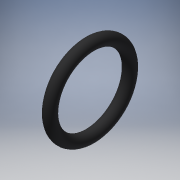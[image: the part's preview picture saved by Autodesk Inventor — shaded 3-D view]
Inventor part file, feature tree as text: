
AUTODESK INVENTOR PART (.ipt)
format: ipt  version: 2019.4 (Build 234330000, 330)  size: 146,432 bytes
history: native  units: in
note: dims shown in document units (in); Inventor stores cm internally (conversion verified against a paired STEP export)
features: sketch x2, sweep x1
ambient origin geometry x8: Origin, YZ Plane, XZ Plane, XY Plane, X Axis, Y Axis, Z Axis, Center Point
bodies: Solid1 (feature_tree)
feature tree (3):
  sweep  "Sweep1"
  sketch  "Sketch1"  dims[d0=0.103in d1=0.612in]
  sketch  "Sketch2"  dims[d2=0.0in d3=0.0in]
